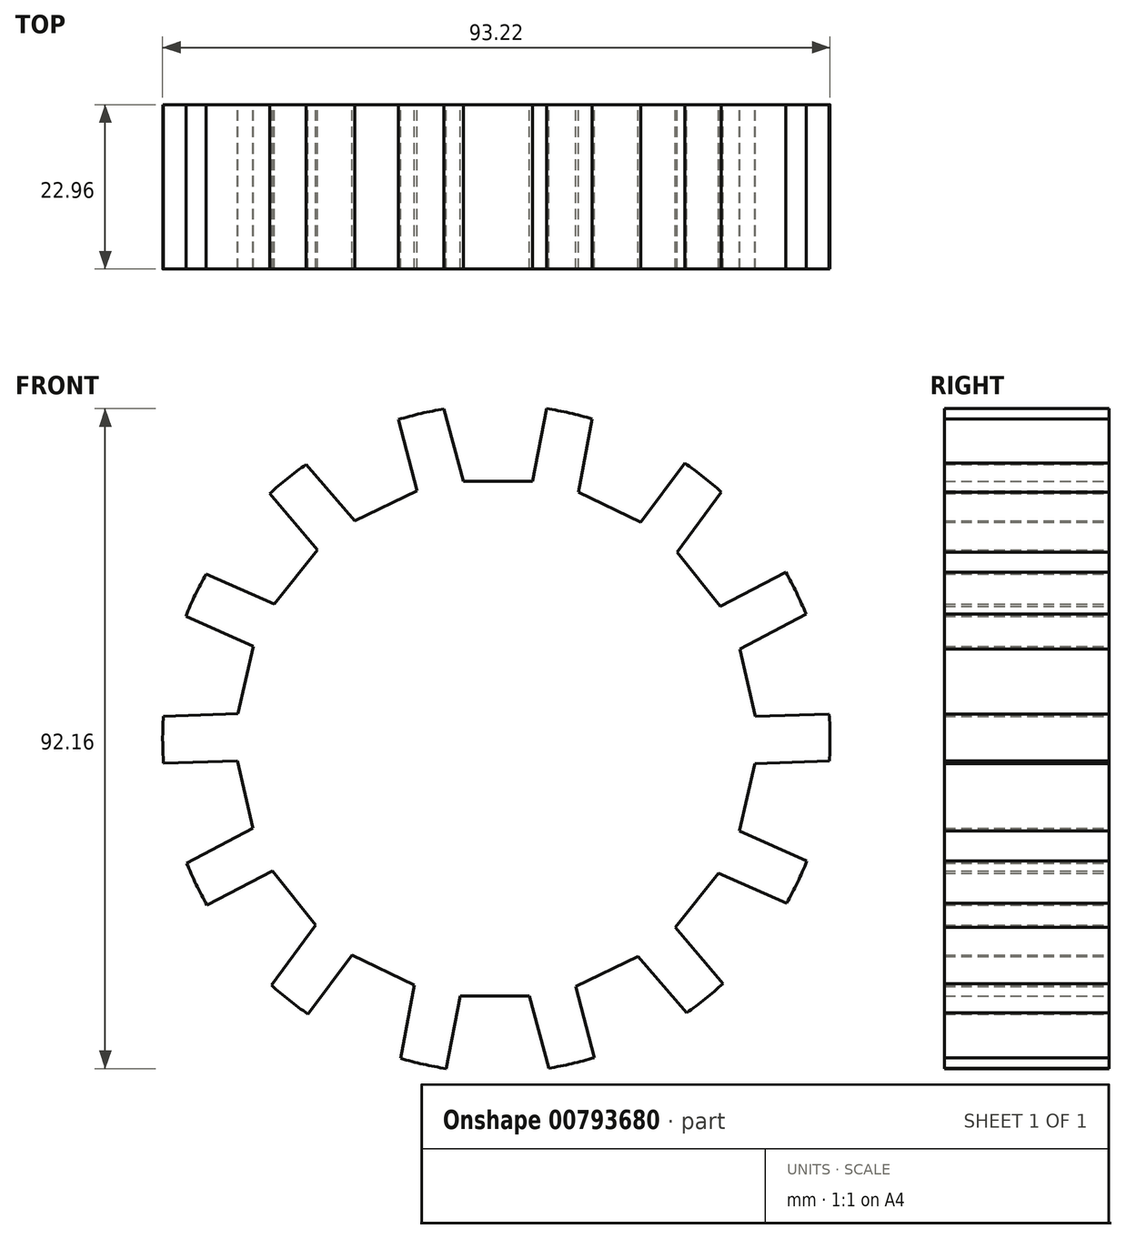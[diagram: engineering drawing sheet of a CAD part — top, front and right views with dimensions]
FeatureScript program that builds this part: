
annotation { "Feature Type Name" : "Feature", "Feature Type Description" : "" }
export const myFeature = defineFeature(function(context is Context, id is Id, definition is map)
    precondition{}
    {
        {
            var Q0;
            Q0=qCreatedBy(makeId("Right.planeOp"),FACE);
            var sketch = newSketch(context, id + "F0", { "sketchPlane" : qUnion([Q0])});
            skLineSegment(sketch, "E0.bottom", {"start": v(0, 0) * mm, "end": v(22.96, 0) * mm});
            skLineSegment(sketch, "E0.top", {"start": v(0, 46.6) * mm, "end": v(22.96, 46.6) * mm});
            skLineSegment(sketch, "E0.left", {"start": v(0, 0) * mm, "end": v(0, 46.6) * mm});
            skLineSegment(sketch, "E0.right", {"start": v(22.96, 0) * mm, "end": v(22.96, 46.6) * mm});
            skSolve(sketch);
        }
        {
            var Q0;
            Q0=makeQuery(id+"F0.imprint","IMPRINT",FACE,{"disambiguationData":[TD([[makeQuery(id+"F0.imprint","IMPRINT",EDGE,{"derivedFrom":sQuery(id+"F0.wireOp",EDGE,"E0.bottom")}),1.0]])]});
            var Q1;
            Q1=sQuery(id+"F0.wireOp",EDGE,"E0.bottom");
            revolve(context, id + "F1", {"surfaceOperationType" : NewSurfaceOperationType.NEW, "entities" : qUnion([Q0]), "axis" : qUnion([Q1]), "revolveType" : RevolveType.FULL});
        }
        {
            var Q0;
            Q0=makeQuery(id+"F1.opRevolve","SWEPT_FACE",FACE,{"disambiguationData":[OSD([sQuery(id+"F0.wireOp",EDGE,"E0.right")])]});
            var sketch = newSketch(context, id + "F2", { "sketchPlane" : qUnion([Q0])});
            skLineSegment(sketch, "E1", {"start": v(-7, 46.08) * mm, "end": v(-5.03, 35.97) * mm});
            skLineSegment(sketch, "E2", {"start": v(-5.03, 35.97) * mm, "end": v(0, 35.97) * mm});
            skLineSegment(sketch, "E3", {"start": v(0, 35.97) * mm, "end": v(4.63, 35.97) * mm});
            skLineSegment(sketch, "E4", {"start": v(4.63, 35.97) * mm, "end": v(7.31, 46.03) * mm});
            skSolve(sketch);
        }
        {
            var Q0;
            {var subQ1=sQuery(id+"F2.wireOp",EDGE,"E1");Q0=makeQuery(id+"F2.imprint","IMPRINT",FACE,{"disambiguationData":[TD([[makeQuery(id+"F2.imprint","IMPRINT",EDGE,{"derivedFrom":subQ1}),1.0]])]});}
            extrude(context, id + "F3", {"entities" : qUnion([Q0]), "operationType" : NewBodyOperationType.REMOVE, "oppositeDirection" : true, "depth" : 25.4 * mm, "offsetDistance" : 25.4 * mm});
        }
        {
            var Q0;
            Q0=makeQuery(id+"F3.boolean.opBoolean","COPY",FACE,{"derivedFrom":makeQuery(id+"F3.opExtrude","SWEPT_FACE",FACE,{"disambiguationData":[OSD([sQuery(id+"F2.wireOp",EDGE,"E4")])]})});
            var Q1;
            Q1=makeQuery(id+"F3.boolean.opBoolean","COPY",FACE,{"derivedFrom":makeQuery(id+"F3.opExtrude","SWEPT_FACE",FACE,{"disambiguationData":[OSD([sQuery(id+"F2.wireOp",EDGE,"E2"),sQuery(id+"F2.wireOp",EDGE,"E3")])]})});
            var Q2;
            Q2=makeQuery(id+"F3.boolean.opBoolean","COPY",FACE,{"derivedFrom":makeQuery(id+"F3.opExtrude","SWEPT_FACE",FACE,{"disambiguationData":[OSD([sQuery(id+"F2.wireOp",EDGE,"E1")])]})});
            var Q3;
            Q3=sQuery(id+"F0.wireOp",EDGE,"E0.bottom");
            circularPattern(context, id + "F4", {"patternType" : PatternType.FACE, "faces" : qUnion([Q0, Q1, Q2]), "axis" : qUnion([Q3]), "angle" : 360 * degree, "instanceCount" : 14, "equalSpace" : true});
        }
    });
